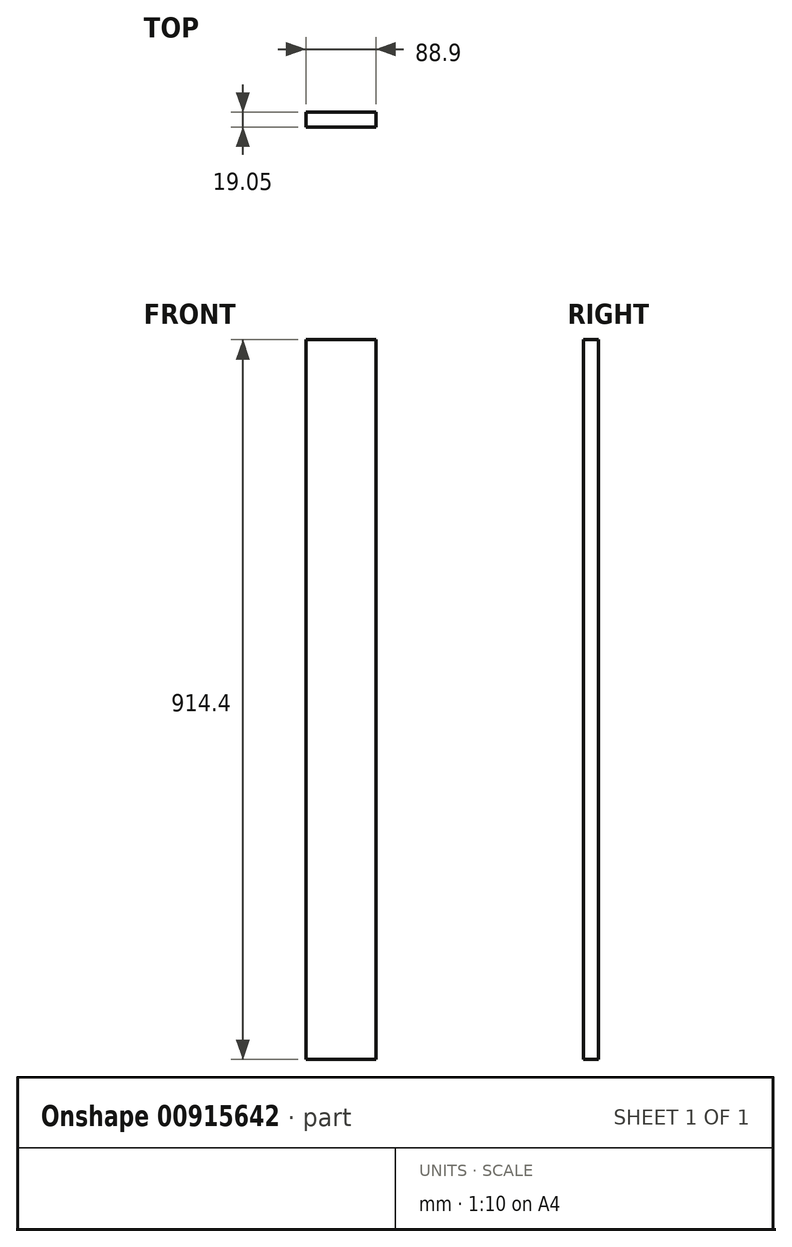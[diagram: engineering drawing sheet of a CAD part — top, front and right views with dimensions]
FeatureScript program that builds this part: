
annotation { "Feature Type Name" : "Feature", "Feature Type Description" : "" }
export const myFeature = defineFeature(function(context is Context, id is Id, definition is map)
    precondition{}
    {
        {
            var Q0;
            Q0=qCreatedBy(makeId("Front.planeOp"),FACE);
            var sketch = newSketch(context, id + "F0", { "sketchPlane" : qUnion([Q0])});
            skLineSegment(sketch, "E0.bottom", {"start": v(44.45, 457.2) * mm, "end": v(-44.45, 457.2) * mm});
            skLineSegment(sketch, "E0.top", {"start": v(44.45, -457.2) * mm, "end": v(-44.45, -457.2) * mm});
            skLineSegment(sketch, "E0.left", {"start": v(44.45, 457.2) * mm, "end": v(44.45, -457.2) * mm});
            skLineSegment(sketch, "E0.right", {"start": v(-44.45, 457.2) * mm, "end": v(-44.45, -457.2) * mm});
            skPoint(sketch, "E0.middle", {"position": v(0, 0) * mm});
            skSolve(sketch);
        }
        {
            var Q0;
            Q0 = qSketchRegion(id + "F0", true);
            extrude(context, id + "F1", {"entities" : qUnion([Q0]), "depth" : 19.05 * mm, "offsetDistance" : 25.4 * mm});
        }
    });
